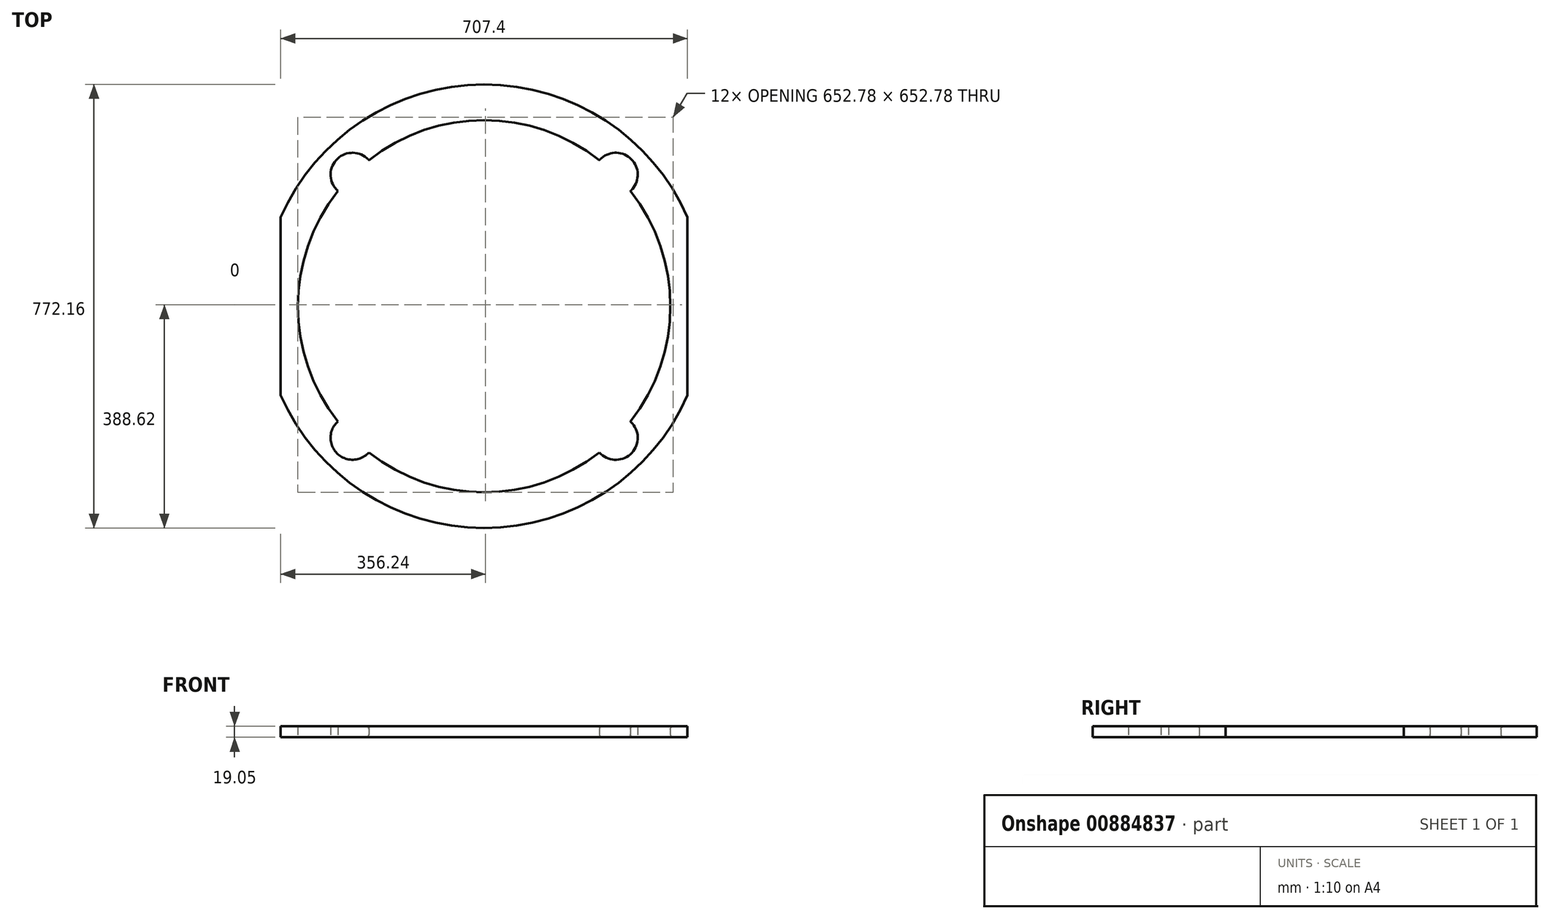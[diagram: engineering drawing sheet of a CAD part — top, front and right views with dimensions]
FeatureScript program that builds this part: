
annotation { "Feature Type Name" : "Feature", "Feature Type Description" : "" }
export const myFeature = defineFeature(function(context is Context, id is Id, definition is map)
    precondition{}
    {
        {
            var Q0;
            Q0=qCreatedBy(makeId("Top.planeOp"),FACE);
            var sketch = newSketch(context, id + "F0", { "sketchPlane" : qUnion([Q0])});
            skCircle(sketch, "E0", {"center": v(0, 0) * mm, "radius": 323.85 * mm});
            skLineSegment(sketch, "E1", {"start": v(0, 0) * mm, "end": v(0, 386.08) * mm, "construction": true});
            skLineSegment(sketch, "E2", {"start": v(0, 0) * mm, "end": v(0, -386.08) * mm, "construction": true});
            skLineSegment(sketch, "E3", {"start": v(0, 0) * mm, "end": v(229, 229) * mm, "construction": true});
            skArc(sketch, "E4", {"start": v(254.3, 200.52) * mm, "mid": v(255.94, 255.94) * mm, "end": v(200.52, 254.3) * mm});
            skLineSegment(sketch, "E5.trimOffspring", {"start": v(255.94, 255.94) * mm, "end": v(273, 273) * mm, "construction": true});
            skArc(sketch, "E6.MirrorCS", {"start": v(-254.3, 200.52) * mm, "mid": v(-255.94, 255.94) * mm, "end": v(-200.52, 254.3) * mm});
            skLineSegment(sketch, "E7", {"start": v(323.85, 0) * mm, "end": v(-323.85, 0) * mm, "construction": true});
            skArc(sketch, "E8.MirrorCS", {"start": v(254.3, -200.52) * mm, "mid": v(255.94, -255.94) * mm, "end": v(200.52, -254.3) * mm});
            skArc(sketch, "E9.MirrorCS", {"start": v(-254.3, -200.52) * mm, "mid": v(-255.94, -255.94) * mm, "end": v(-200.52, -254.3) * mm});
            skArc(sketch, "E10", {"start": v(-353.7, -154.78) * mm, "mid": v(0, -386.08) * mm, "end": v(353.7, -154.78) * mm});
            skPoint(sketch, "E11", {"position": v(-353.7, 0) * mm});
            skLineSegment(sketch, "E12", {"start": v(-353.7, 0) * mm, "end": v(-353.7, 154.78) * mm});
            skLineSegment(sketch, "E13.MirrorCS", {"start": v(-353.7, 0) * mm, "end": v(-353.7, -154.78) * mm});
            skLineSegment(sketch, "E14.MirrorCS", {"start": v(353.7, 0) * mm, "end": v(353.7, 154.78) * mm});
            skLineSegment(sketch, "E15.MirrorCS", {"start": v(353.7, 0) * mm, "end": v(353.7, -154.78) * mm});
            skPoint(sketch, "E16.orphan", {"position": v(-353.7, 177.8) * mm});
            skPoint(sketch, "E17.orphan", {"position": v(-353.7, -177.8) * mm});
            skArc(sketch, "E18.trimOffspring", {"start": v(353.7, 154.78) * mm, "mid": v(0, 386.08) * mm, "end": v(-353.7, 154.78) * mm});
            skSolve(sketch);
        }
        {
            var Q0;
            Q0 = qSketchRegion(id + "F0", true);
            extrude(context, id + "F1", {"entities" : qUnion([Q0]), "depth" : 19.05 * mm, "offsetDistance" : 25.4 * mm});
        }
        {
            var Q0;
            {var subQ0=sQuery(id+"F0.wireOp",EDGE,"E0");Q0=makeQuery(id+"F1.opExtrude","CAP_EDGE",EDGE,{"disambiguationData":[OSD([subQ0]),TDD([makeQuery(id+"F0.imprint","IMPRINT",EDGE,{"disambiguationData":[TD([[makeQuery(id+"F0.imprint","INTERSECT",VERTEX,{"disambiguationData":[OD(1.0)],"derivedFrom":[subQ0,sQuery(id+"F0.wireOp",EDGE,"E4")]}),-1.0]])],"derivedFrom":subQ0})])],"isStart":false});}
            var Q1;
            {var subQ0=sQuery(id+"F0.wireOp",EDGE,"E0");Q1=makeQuery(id+"F1.opExtrude","CAP_EDGE",EDGE,{"disambiguationData":[OSD([subQ0]),TDD([makeQuery(id+"F0.imprint","IMPRINT",EDGE,{"disambiguationData":[TD([[makeQuery(id+"F0.imprint","INTERSECT",VERTEX,{"disambiguationData":[OD(0.0)],"derivedFrom":[subQ0,sQuery(id+"F0.wireOp",EDGE,"E6.MirrorCS")]}),-1.0]])],"derivedFrom":subQ0})])],"isStart":false});}
            var Q2;
            {var subQ0=sQuery(id+"F0.wireOp",EDGE,"E0");Q2=makeQuery(id+"F1.opExtrude","CAP_EDGE",EDGE,{"disambiguationData":[OSD([subQ0]),TDD([makeQuery(id+"F0.imprint","IMPRINT",EDGE,{"disambiguationData":[TD([[makeQuery(id+"F0.imprint","INTERSECT",VERTEX,{"disambiguationData":[OD(1.0)],"derivedFrom":[subQ0,sQuery(id+"F0.wireOp",EDGE,"E8.MirrorCS")]}),1.0]])],"derivedFrom":subQ0})])],"isStart":false});}
            var Q3;
            {var subQ0=sQuery(id+"F0.wireOp",EDGE,"E0");Q3=makeQuery(id+"F1.opExtrude","CAP_EDGE",EDGE,{"disambiguationData":[OSD([subQ0]),TDD([makeQuery(id+"F0.imprint","IMPRINT",EDGE,{"disambiguationData":[TD([[makeQuery(id+"F0.imprint","INTERSECT",VERTEX,{"disambiguationData":[OD(0.0)],"derivedFrom":[subQ0,sQuery(id+"F0.wireOp",EDGE,"E4")]}),1.0]])],"derivedFrom":subQ0})])],"isStart":false});}
            var Q4;
            {var subQ0=sQuery(id+"F0.wireOp",EDGE,"E0");Q4=makeQuery(id+"F1.opExtrude","CAP_EDGE",EDGE,{"disambiguationData":[OSD([subQ0]),TDD([makeQuery(id+"F0.imprint","IMPRINT",EDGE,{"disambiguationData":[TD([[makeQuery(id+"F0.imprint","INTERSECT",VERTEX,{"disambiguationData":[OD(0.0)],"derivedFrom":[subQ0,sQuery(id+"F0.wireOp",EDGE,"E6.MirrorCS")]}),-1.0]])],"derivedFrom":subQ0})])],"isStart":true});}
            var Q5;
            {var subQ0=sQuery(id+"F0.wireOp",EDGE,"E0");Q5=makeQuery(id+"F1.opExtrude","CAP_EDGE",EDGE,{"disambiguationData":[OSD([subQ0]),TDD([makeQuery(id+"F0.imprint","IMPRINT",EDGE,{"disambiguationData":[TD([[makeQuery(id+"F0.imprint","INTERSECT",VERTEX,{"disambiguationData":[OD(1.0)],"derivedFrom":[subQ0,sQuery(id+"F0.wireOp",EDGE,"E4")]}),-1.0]])],"derivedFrom":subQ0})])],"isStart":true});}
            var Q6;
            {var subQ0=sQuery(id+"F0.wireOp",EDGE,"E0");Q6=makeQuery(id+"F1.opExtrude","CAP_EDGE",EDGE,{"disambiguationData":[OSD([subQ0]),TDD([makeQuery(id+"F0.imprint","IMPRINT",EDGE,{"disambiguationData":[TD([[makeQuery(id+"F0.imprint","INTERSECT",VERTEX,{"disambiguationData":[OD(0.0)],"derivedFrom":[subQ0,sQuery(id+"F0.wireOp",EDGE,"E4")]}),1.0]])],"derivedFrom":subQ0})])],"isStart":true});}
            var Q7;
            {var subQ0=sQuery(id+"F0.wireOp",EDGE,"E0");Q7=makeQuery(id+"F1.opExtrude","CAP_EDGE",EDGE,{"disambiguationData":[OSD([subQ0]),TDD([makeQuery(id+"F0.imprint","IMPRINT",EDGE,{"disambiguationData":[TD([[makeQuery(id+"F0.imprint","INTERSECT",VERTEX,{"disambiguationData":[OD(1.0)],"derivedFrom":[subQ0,sQuery(id+"F0.wireOp",EDGE,"E8.MirrorCS")]}),1.0]])],"derivedFrom":subQ0})])],"isStart":true});}
            fillet(context, id + "F2", {"entities" : qUnion([Q0, Q1, Q2, Q3, Q4, Q5, Q6, Q7]), "radius" : 5.08 * mm, "tangentPropagation" : true, "allowEdgeOverflow" : false});
        }
    });
